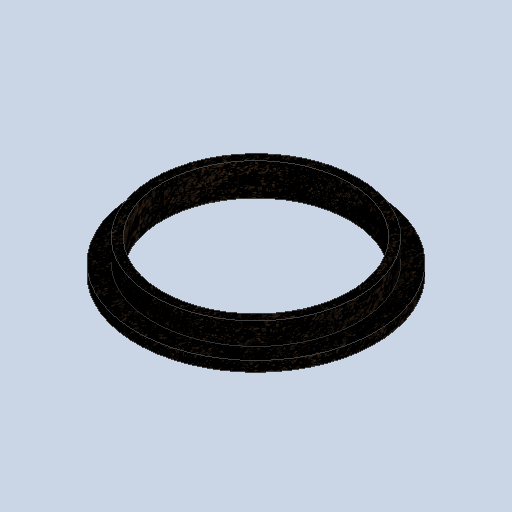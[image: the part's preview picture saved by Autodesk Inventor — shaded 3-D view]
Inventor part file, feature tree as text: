
AUTODESK INVENTOR PART (.ipt)
format: ipt  version: 2025.1 (Build 291241000, 241)  size: 137,728 bytes
history: native  units: mm
features: other x3, sketch x2
ambient origin geometry x8: Origin, YZ Plane, XZ Plane, XY Plane, X Axis, Y Axis, Z Axis, Center Point
bodies: Solid1 (feature_tree)
feature tree (5):
  other  "glassSchutz.ipt"
  other  "Solid1::glassSchutz.ipt"
  other  "TaggingFeature1"
  sketch  "Sketch1"  dims[d0=10.0mm]
  sketch  "Sketch2"
